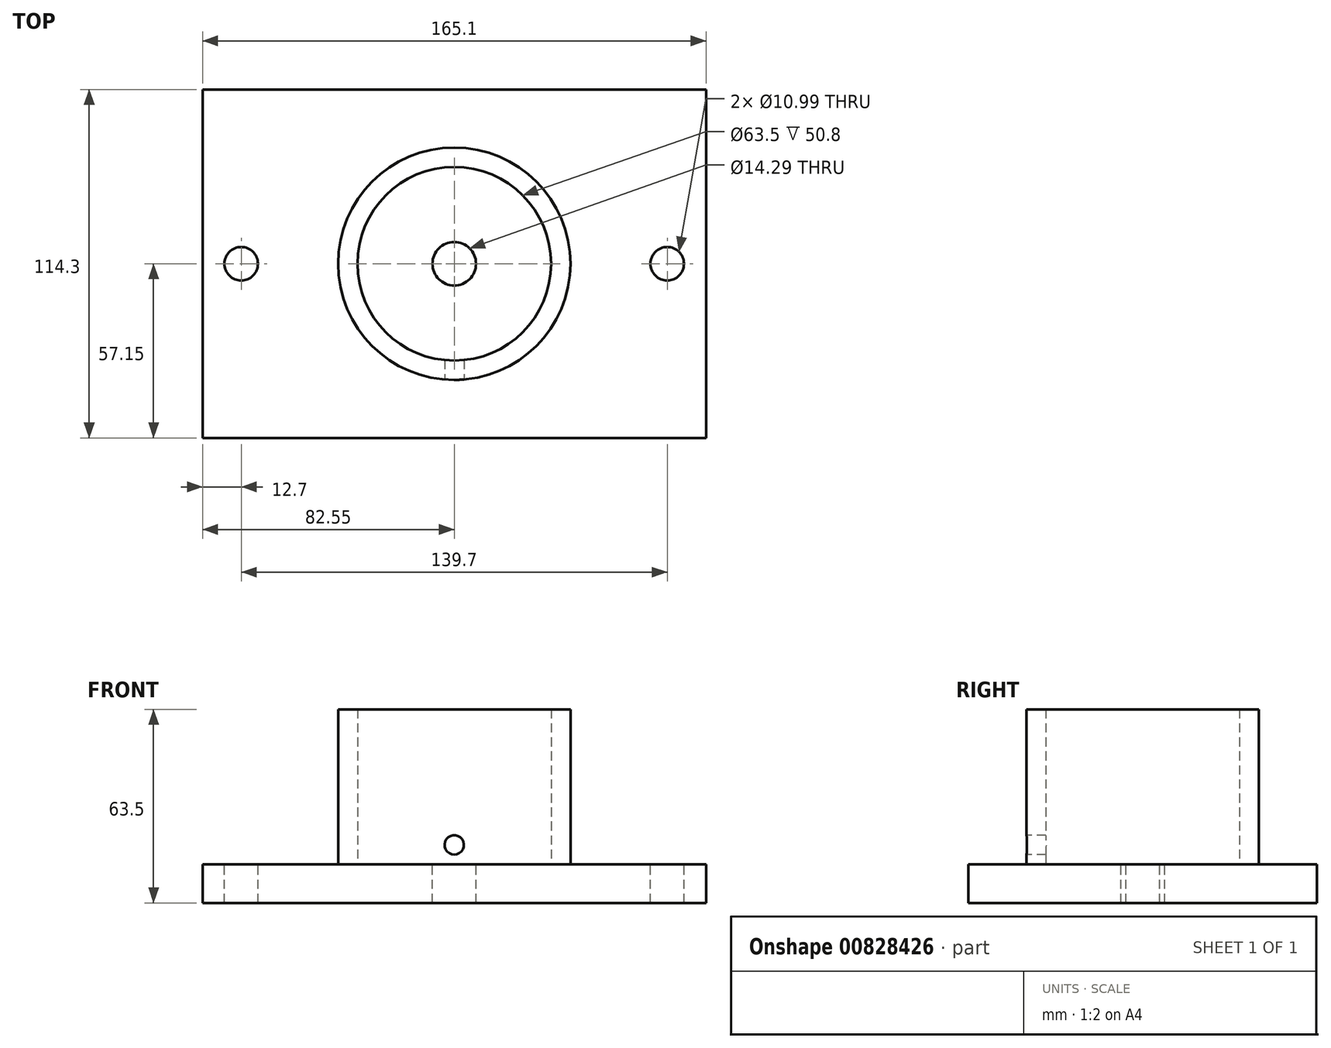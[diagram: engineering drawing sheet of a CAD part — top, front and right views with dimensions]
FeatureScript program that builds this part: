
annotation { "Feature Type Name" : "Feature", "Feature Type Description" : "" }
export const myFeature = defineFeature(function(context is Context, id is Id, definition is map)
    precondition{}
    {
        {
            var Q0;
            Q0=qCreatedBy(makeId("Top.planeOp"),FACE);
            var sketch = newSketch(context, id + "F0", { "sketchPlane" : qUnion([Q0])});
            skLineSegment(sketch, "E0.bottom", {"start": v(0, 0) * mm, "end": v(165.1, 0) * mm});
            skLineSegment(sketch, "E0.top", {"start": v(0, 114.3) * mm, "end": v(165.1, 114.3) * mm});
            skLineSegment(sketch, "E0.left", {"start": v(0, 0) * mm, "end": v(0, 114.3) * mm});
            skLineSegment(sketch, "E0.right", {"start": v(165.1, 0) * mm, "end": v(165.1, 114.3) * mm});
            skSolve(sketch);
        }
        {
            var Q0;
            Q0 = qSketchRegion(id + "F0", true);
            extrude(context, id + "F1", {"entities" : qUnion([Q0]), "depth" : 12.7 * mm, "offsetDistance" : 25.4 * mm});
        }
        {
            var Q0;
            Q0=makeQuery(id+"F1.opExtrude","CAP_FACE",FACE,{"disambiguationData":[OSD([sQuery(id+"F0.wireOp",EDGE,"E0.bottom"),sQuery(id+"F0.wireOp",EDGE,"E0.top"),sQuery(id+"F0.wireOp",EDGE,"E0.left"),sQuery(id+"F0.wireOp",EDGE,"E0.right")])],"isStart":false});
            var sketch = newSketch(context, id + "F2", { "sketchPlane" : qUnion([Q0])});
            skCircle(sketch, "E1", {"center": v(82.55, 57.15) * mm, "radius": 31.75 * mm});
            skCircle(sketch, "E2", {"center": v(82.55, 57.15) * mm, "radius": 38.1 * mm});
            skSolve(sketch);
        }
        {
            var Q0;
            Q0 = qSketchRegion(id + "F2", true);
            extrude(context, id + "F3", {"entities" : qUnion([Q0]), "operationType" : NewBodyOperationType.ADD, "depth" : 50.8 * mm, "offsetDistance" : 25.4 * mm});
        }
        {
            var Q0;
            {var subQ0=sQuery(id+"F0.wireOp",EDGE,"E0.left");var subQ1=sQuery(id+"F0.wireOp",EDGE,"E0.top");var subQ2=sQuery(id+"F0.wireOp",EDGE,"E0.right");var subQ3=sQuery(id+"F0.wireOp",EDGE,"E0.bottom");Q0=makeQuery(id+"F3.boolean.opBoolean","SPLIT",FACE,{"disambiguationData":[TD([makeQuery(id+"F1.opExtrude","SWEPT_FACE",FACE,{"disambiguationData":[OSD([subQ3])]})])],"derivedFrom":makeQuery(id+"F1.opExtrude","CAP_FACE",FACE,{"disambiguationData":[OSD([subQ3,subQ1,subQ0,subQ2])],"isStart":false})});}
            var sketch = newSketch(context, id + "F4", { "sketchPlane" : qUnion([Q0])});
            skCircle(sketch, "E3", {"center": v(152.4, 57.15) * mm, "radius": 5.5 * mm});
            skCircle(sketch, "E4", {"center": v(12.7, 57.15) * mm, "radius": 5.5 * mm});
            skPoint(sketch, "E4.centerSnap0", {"position": v(0, 57.15) * mm});
            skCircle(sketch, "E5", {"center": v(82.55, 57.15) * mm, "radius": 7.14 * mm});
            skSolve(sketch);
        }
        {
            var Q0;
            Q0 = qSketchRegion(id + "F4", true);
            extrude(context, id + "F5", {"entities" : qUnion([Q0]), "operationType" : NewBodyOperationType.REMOVE, "oppositeDirection" : true, "depth" : 25.4 * mm, "offsetDistance" : 25.4 * mm});
        }
        {
            var Q0;
            Q0=qCreatedBy(makeId("Front.planeOp"),FACE);
            var sketch = newSketch(context, id + "F6", { "sketchPlane" : qUnion([Q0])});
            skLineSegment(sketch, "E6", {"start": v(0, 0) * mm, "end": v(0, 19.05) * mm});
            skLineSegment(sketch, "E7", {"start": v(0, 19.05) * mm, "end": v(82.55, 19.05) * mm});
            skCircle(sketch, "E8", {"center": v(82.55, 19.05) * mm, "radius": 3.18 * mm});
            skSolve(sketch);
        }
        {
            var Q0;
            Q0 = qSketchRegion(id + "F6", true);
            extrude(context, id + "F7", {"entities" : qUnion([Q0]), "operationType" : NewBodyOperationType.REMOVE, "oppositeDirection" : true, "depth" : 76.2 * mm, "offsetDistance" : 25.4 * mm});
        }
    });
